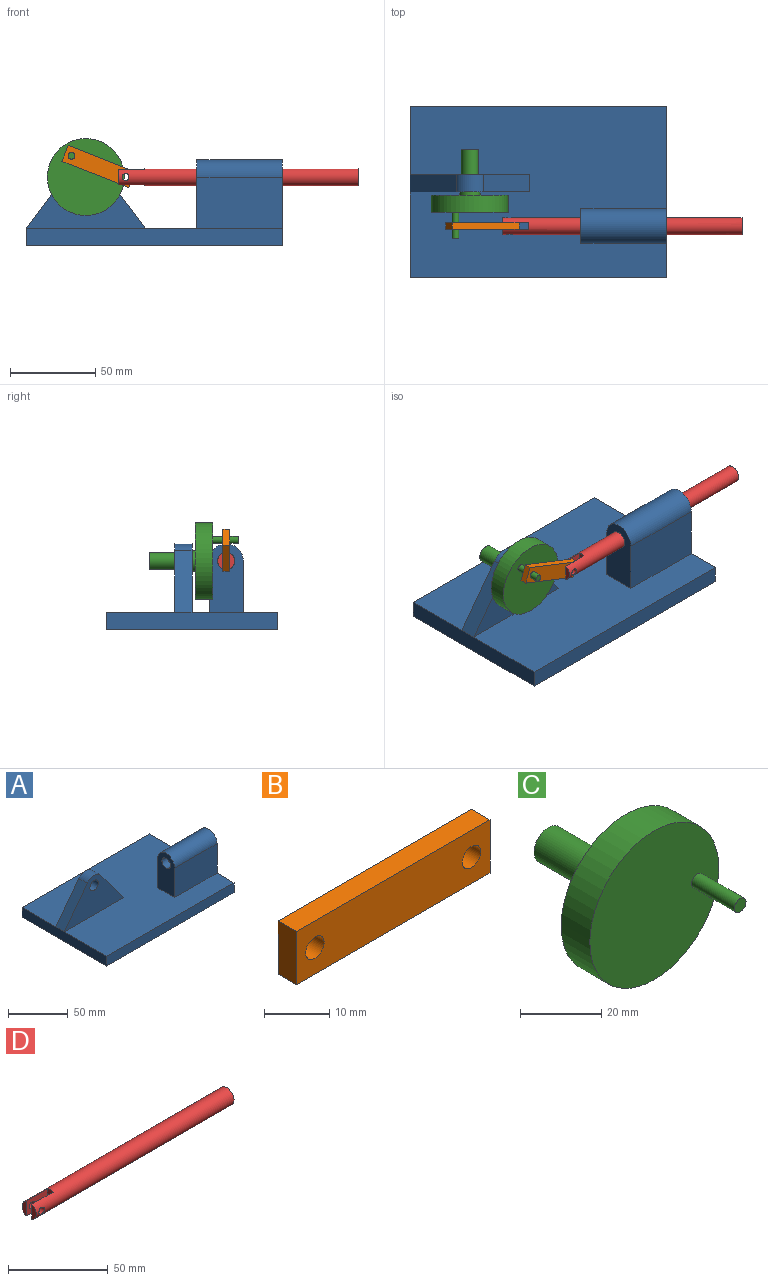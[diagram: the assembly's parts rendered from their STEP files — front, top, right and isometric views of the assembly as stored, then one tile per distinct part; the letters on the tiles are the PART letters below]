
ASSEMBLY  parts=4 mates=4
PART A: 17 faces, bbox 150x100x50 mm
  f0: plane 150x100mm, normal (0,0,1), area 13300mm2, adj f1,f3,f4,f5,f6,f10,f11,f12
  f1: plane 100x10mm, normal (-1,0,0), area 1000mm2, adj f0,f2,f4,f5,f8
  f2: plane 150x100mm, normal (0,0,-1), area 15000mm2, adj f1,f3,f4,f5
  f3: plane 100x50mm, normal (1,0,0), area 1678.5mm2, adj f0,f2,f4,f5,f12,f13,f15,f16
  f4: plane 150x10mm, normal (0,-1,0), area 1500mm2, adj f0,f1,f2,f3
  f5: plane 150x10mm, normal (0,1,0), area 1500mm2, adj f0,f1,f2,f3
  f6: plane 36x27mm, normal (0.8,0,0.6), area 450mm2, adj f0,f7,f10,f11
  f7: cylinder r=10mm len=16mm, axis (0,-1,0), area 185.5mm2, adj f6,f8,f10,f11
  f8: plane 36x27mm, normal (-0.8,0,0.6), area 450mm2, adj f1,f7,f10,f11
  f9: cylinder r=5mm len=10mm, axis (0,-1,0), area 314.2mm2, adj f10,f11
  f10: plane 70x40mm, normal (0,1,0), area 1514.2mm2, adj f0,f6,f7,f8,f9
  f11: plane 70x40mm, normal (0,-1,0), area 1514.2mm2, adj f0,f6,f7,f8,f9
  f12: plane 50x30mm, normal (0,-1,0), area 1500mm2, adj f0,f3,f14,f15
  f13: plane 50x30mm, normal (0,1,0), area 1500mm2, adj f0,f3,f14,f15
  f14: plane 40x20mm, normal (-1,0,0), area 678.5mm2, adj f0,f12,f13,f15,f16
  f15: cylinder r=10mm len=50mm, axis (1,0,0), area 1570.8mm2, adj f3,f12,f13,f14
  f16: cylinder r=5mm len=50mm, axis (1,0,0), area 1570.8mm2, adj f3,f14
PART B: 8 faces, bbox 42x4x10 mm
  f0: plane 42x10mm, normal (0,-1,0), area 394.9mm2, adj f1,f3,f4,f5,f6,f7
  f1: plane 42x4mm, normal (0,0,1), area 168mm2, adj f0,f2,f4,f5
  f2: plane 42x10mm, normal (0,1,0), area 394.9mm2, adj f1,f3,f4,f5,f6,f7
  f3: cylinder r=2mm len=4mm, axis (0,1,0), area 50.3mm2, adj f0,f2
  f4: plane 10x4mm, normal (-1,0,0), area 40mm2, adj f0,f1,f2,f6
  f5: plane 10x4mm, normal (1,0,0), area 40mm2, adj f0,f1,f2,f6
  f6: plane 42x4mm, normal (0,0,-1), area 168mm2, adj f0,f2,f4,f5
  f7: cylinder r=2mm len=4mm, axis (0,1,0), area 50.3mm2, adj f0,f2
PART C: 9 faces, bbox 45x52x45 mm
  f0: cylinder r=5mm len=25mm, axis (0,-1,0), area 785.4mm2, adj f1,f3
  f1: plane 10x10mm, normal (0,1,0), area 78.5mm2, adj f0
  f2: cylinder r=6mm len=12mm, axis (0,1,0), area 75.4mm2, adj f3,f6
  f3: plane 12x12mm, normal (0,1,0), area 34.6mm2, adj f0,f2
  f4: cylinder r=22.5mm len=45mm, axis (0,1,0), area 1413.7mm2, adj f5,f6
  f5: plane 45x45mm, normal (0,-1,0), area 1577.9mm2, adj f4,f7
  f6: plane 45x45mm, normal (0,1,0), area 1477.3mm2, adj f2,f4
  f7: cylinder r=2mm len=15mm, axis (0,1,0), area 188.5mm2, adj f5,f8
  f8: plane 4x4mm, normal (0,-1,0), area 12.6mm2, adj f7
PART D: 9 faces, bbox 140x10x10 mm
  f0: plane 9.17x3mm, normal (-1,0,0), area 19.8mm2, adj f1,f4
  f1: cylinder r=5mm len=140mm, axis (1,0,0), area 4249.1mm2, adj f0,f2,f3,f4,f5,f6,f7,f8
  f2: plane 9.17x3mm, normal (-1,0,0), area 19.8mm2, adj f1,f5
  f3: plane 10x10mm, normal (1,0,0), area 78.5mm2, adj f1
  f4: plane 15x9.17mm, normal (0,1,0), area 124.9mm2, adj f0,f1,f6,f8
  f5: plane 15x9.17mm, normal (0,-1,0), area 124.9mm2, adj f1,f2,f6,f7
  f6: plane 10x4mm, normal (-1,0,0), area 38.9mm2, adj f1,f4,f5
  f7: cylinder r=2mm len=4mm, axis (0,-1,0), area 35.1mm2, adj f1,f5
  f8: cylinder r=2mm len=4mm, axis (0,-1,0), area 35.1mm2, adj f1,f4
PLACE A at identity fixed
PLACE B rot(axis=(0,1,0),21.4deg) t=(-36.1,0,5.36)mm
PLACE C rot(axis=(0,-1,0),124.2deg) t=(-37.63,0,79.94)mm
PLACE D t=(-25.77,0,0)mm
MATE slider D.f1 <-> A.f15  axis (1,0,0) through (49.23,-20,30)mm
MATE revolute D.f7 <-> B.f3  axis (0,1,0) through (-16.77,-22,30)mm
MATE revolute A.f7 <-> C.f0  axis (0,-1,0) through (-40,0,30)mm
MATE cylindrical B.f7 <-> C.f7  axis (0,-1,0) through (-48.42,-22,42.41)mm
